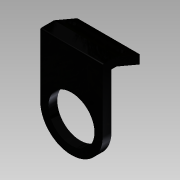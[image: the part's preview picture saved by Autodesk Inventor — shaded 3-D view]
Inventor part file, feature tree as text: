
AUTODESK INVENTOR PART (.ipt)
format: ipt  version: 2015 SP1 (Build 190203100, 203)  size: 140,288 bytes
history: native  units: mm
features: sketch x3, extrude x2, fillet x1, sweep x1
ambient origin geometry x8: Origin, YZ Plane, XZ Plane, XY Plane, X Axis, Y Axis, Z Axis, Center Point
bodies: Body1 (feature_tree)
feature tree (7):
  sketch  "Sketch1"  dims[d28=18.25mm d29=24.75mm d30=24.75mm]
  extrude  "Extrusion5"  Depth=24.75mm
  fillet  "Fillet1"  Radius=24.75mm
  sweep  "Sweep1"
  extrude  "Extrusion7"  TaperAngle=0.0deg  [1 undecoded]
  sketch  "Sketch3"  dims[d36=3.5mm d37=0.0mm d53=0.5mm]
  sketch  "Sketch6"  dims[d54=3.5mm d57=0.0mm d58=0.0mm d67=10.0mm d68=4.014257mm d70=25.0mm d71=25.0mm d72=3.0mm d73=3.0mm d74=3.0mm d75=3.0mm d76=5.0mm d77=5.0mm d78=5.0mm d79=10.0mm d80=0.0mm]
note: 1 required parameter value undecoded (feature->parameter linkage not recoverable at this tier; creation-order binding heuristic only, values carry confidence <= 0.55)
